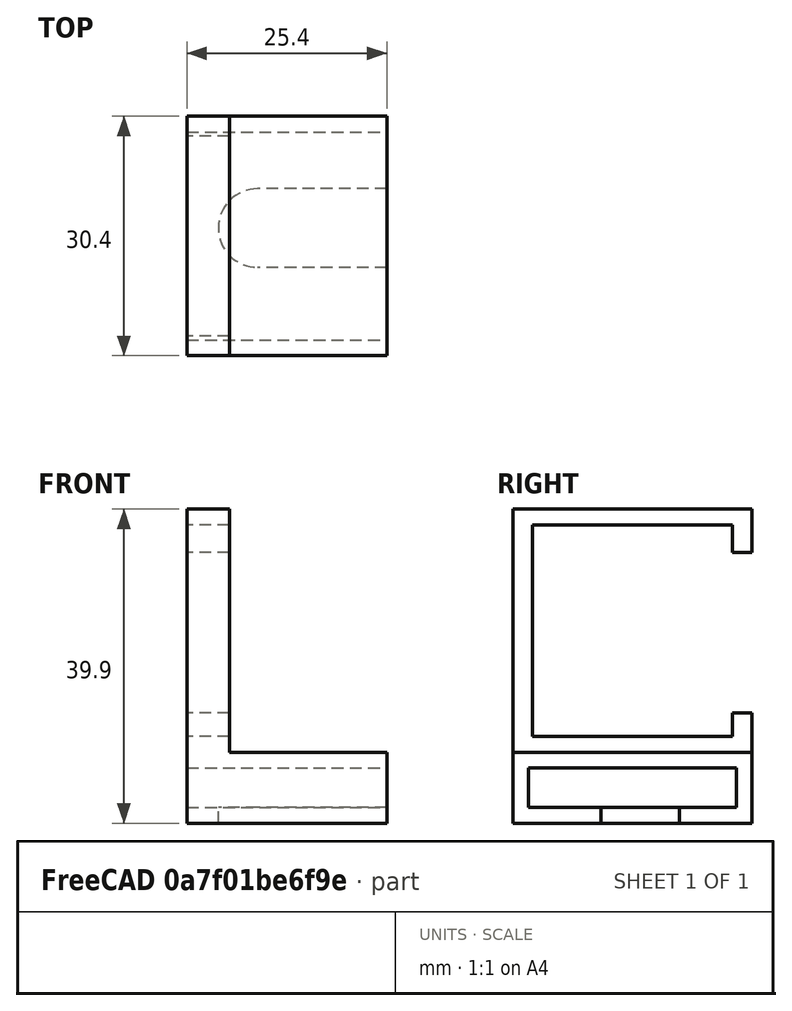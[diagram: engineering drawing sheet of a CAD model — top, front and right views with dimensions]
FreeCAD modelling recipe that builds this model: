
FCSTD DOCUMENT  (FreeCAD 0.18R16146 (Git))
Label: CameraBox
License: All rights reserved
LicenseURL: http://en.wikipedia.org/wiki/All_rights_reserved
objects: Part::Box×8, Part::Cut×4, Part::Fuse×4, Part::Cylinder×1
note: 17 computed .brp shape members not serialized (recipe doc carries the construction recipe); baked Part::Feature solids carry a one-line shape summary decoded from their .brp

FEATURE [Part::Box] Box  label="Top"
  AttacherType = Attacher::AttachEngine3D
  Height = 2
  Length = 25.4
  Placement = pos=(0,0,7) rot=(0,0,1;0rad)
  Width = 30.4
FEATURE [Part::Box] Box001  label="Bottom"
  AttacherType = Attacher::AttachEngine3D
  Height = 2
  Length = 25.4
  Placement = pos=(0,0,10) rot=(0,0,1;0rad)
  Width = 30.4
FEATURE [Part::Box] Box002  label="Left"
  AttacherType = Attacher::AttachEngine3D
  Height = 5
  Length = 25.4
  Placement = pos=(0,0,2) rot=(0,0,1;0rad)
  Width = 2
FEATURE [Part::Box] Box003  label="Right"
  AttacherType = Attacher::AttachEngine3D
  Height = 5
  Length = 25.4
  Placement = pos=(0,28.4,2) rot=(0,0,1;0rad)
  Width = 2
FEATURE [Part::Cylinder] Cylinder
  Angle = 360
  AttacherType = Attacher::AttachEngine3D
  Height = 4
  Placement = pos=(9,16.2,9) rot=(0,0,1;0rad)
  Radius = 5
FEATURE [Part::Cut] Cut
  Base = -> Box001
  Tool = -> Cylinder
FEATURE [Part::Box] Box004  label="Cube"
  AttacherType = Attacher::AttachEngine3D
  Height = 4
  Length = 17
  Placement = pos=(9,11.2,9) rot=(0,0,1;0rad)
  Width = 10
FEATURE [Part::Cut] Cut001  label="Bottom_with_cut"
  Base = -> Cut
  Placement = pos=(0,0,-10) rot=(0,0,1;0rad)
  Tool = -> Box004
FEATURE [Part::Fuse] Fusion
  Base = -> Cut001
  Tool = -> Box002
FEATURE [Part::Fuse] Fusion001
  Base = -> Fusion
  Tool = -> Box003
FEATURE [Part::Fuse] Fusion002  label="Box"
  Base = -> Fusion001
  Tool = -> Box
FEATURE [Part::Box] Box007  label="Cube001"
  AttacherType = Attacher::AttachEngine3D
  Height = 30.4
  Length = 30.9
  Width = 5.4
FEATURE [Part::Box] Box008  label="Bar"
  AttacherType = Attacher::AttachEngine3D
  Height = 25.4
  Length = 26.9
  Placement = pos=(2,0,2.5) rot=(0,0,1;0rad)
  Width = 26
FEATURE [Part::Cut] Cut003
  Base = -> Box007
  Tool = -> Box008
FEATURE [Part::Box] Box009  label="Gap"
  AttacherType = Attacher::AttachEngine3D
  Height = 10
  Length = 20.4
  Placement = pos=(5,0,0) rot=(0,0,1;0rad)
  Width = 25.4
FEATURE [Part::Cut] Cut004  label="Clip"
  Base = -> Cut003
  Placement = pos=(5.4,30.4,9) rot=(0.57735,-0.57735,0.57735;2.0944rad)
  Tool = -> Box009
FEATURE [Part::Fuse] Fusion003
  Base = -> Fusion002
  Tool = -> Cut004
